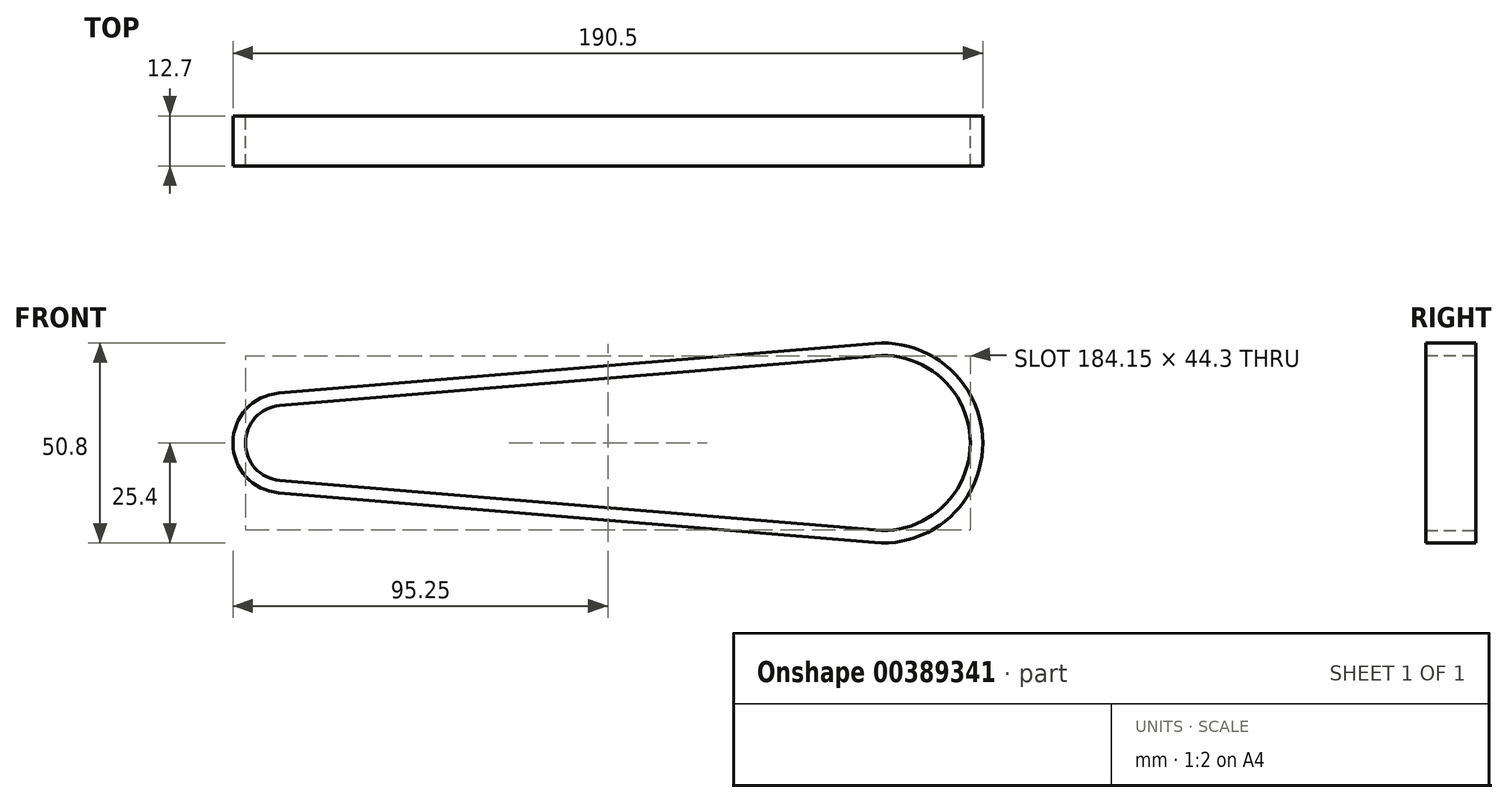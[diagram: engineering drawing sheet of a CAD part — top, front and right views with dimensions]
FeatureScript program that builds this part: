
annotation { "Feature Type Name" : "Feature", "Feature Type Description" : "" }
export const myFeature = defineFeature(function(context is Context, id is Id, definition is map)
    precondition{}
    {
        {
            var Q0;
            Q0=qCreatedBy(makeId("Front.planeOp"),FACE);
            var sketch = newSketch(context, id + "F0", { "sketchPlane" : qUnion([Q0])});
            skArc(sketch, "E0", {"start": v(-0.8, 9.5) * mm, "mid": v(-9.52, 0) * mm, "end": v(-0.8, -9.5) * mm});
            skArc(sketch, "E1", {"start": v(-1.06, 12.66) * mm, "mid": v(-12.7, 0) * mm, "end": v(-1.06, -12.66) * mm});
            skArc(sketch, "E2", {"start": v(150.28, -25.31) * mm, "mid": v(177.8, 0) * mm, "end": v(150.28, 25.31) * mm});
            skArc(sketch, "E3", {"start": v(150.55, -22.15) * mm, "mid": v(174.62, 0) * mm, "end": v(150.55, 22.15) * mm});
            skLineSegment(sketch, "E4", {"start": v(-1.06, 12.66) * mm, "end": v(150.28, 25.31) * mm});
            skLineSegment(sketch, "E5", {"start": v(-1.06, -12.66) * mm, "end": v(150.28, -25.31) * mm});
            skLineSegment(sketch, "E6", {"start": v(-0.8, 9.5) * mm, "end": v(150.55, 22.15) * mm});
            skLineSegment(sketch, "E7", {"start": v(-0.8, -9.5) * mm, "end": v(150.55, -22.15) * mm});
            skSolve(sketch);
        }
        {
            var Q0;
            Q0 = qSketchRegion(id + "F0", true);
            extrude(context, id + "F1", {"entities" : qUnion([Q0]), "depth" : 12.7 * mm});
        }
    });
